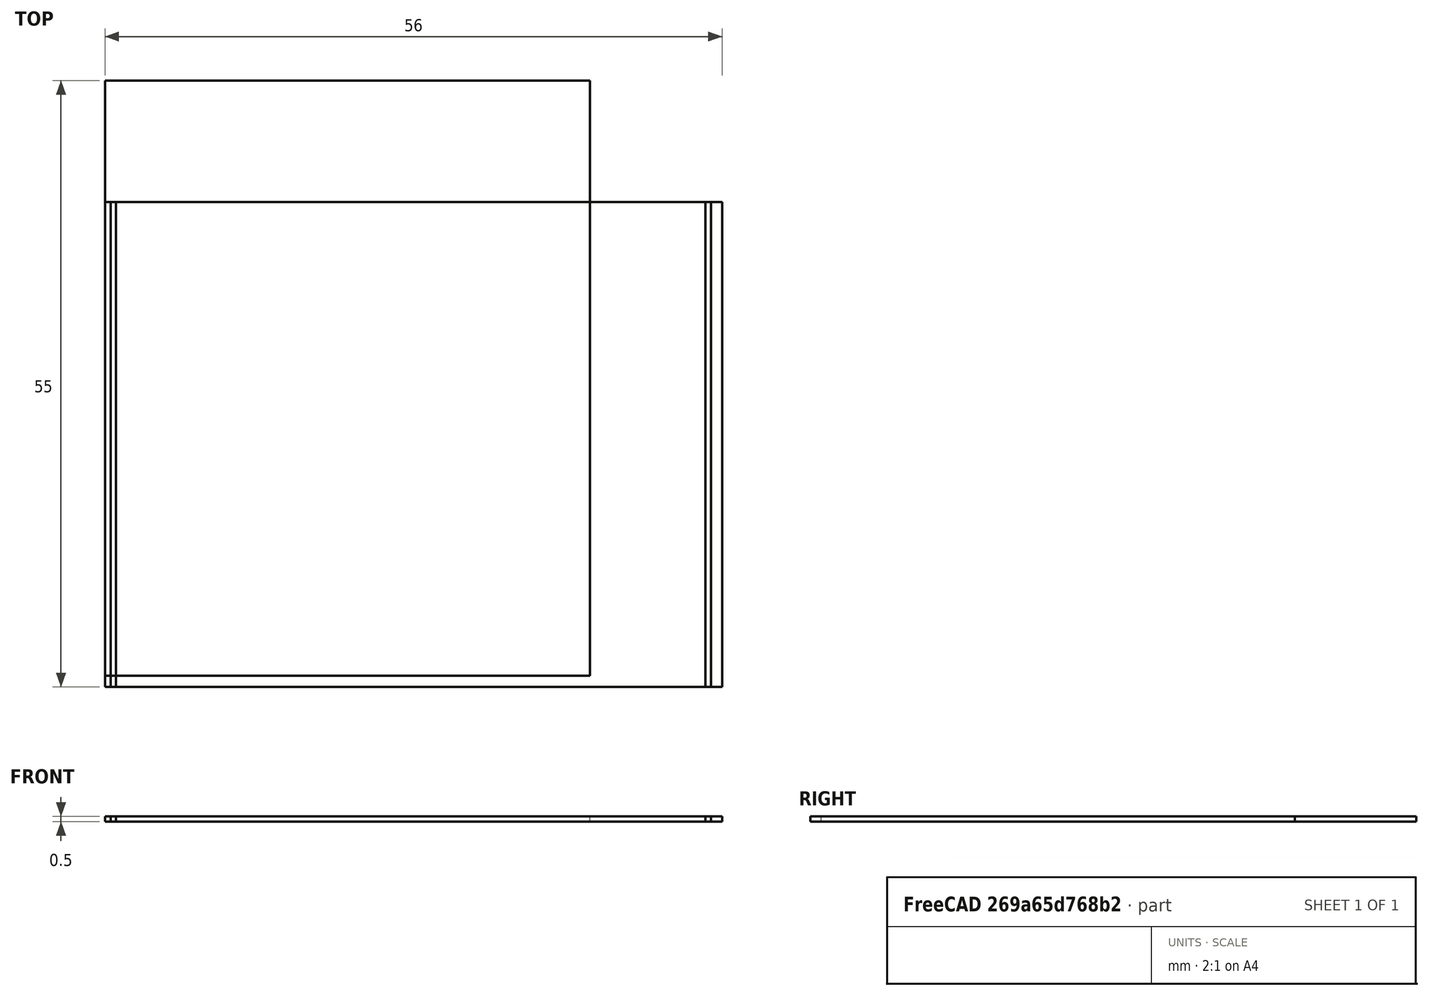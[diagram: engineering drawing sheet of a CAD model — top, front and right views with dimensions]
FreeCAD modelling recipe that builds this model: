
FCSTD DOCUMENT  (FreeCAD 1.0R39109 (Git))
Label: Tea_Light_Lithopane_MA_logo
License: All rights reserved
LicenseURL: http://www.ohwr.org/attachments/2388/cern_ohl_v_1_2.txt
objects: App::FeaturePython×8, Sketcher::SketchObject×4, PartDesign::Pad×4, PartDesign::Body×4, Mesh::Feature×4
note: 24 computed .brp shape members not serialized (recipe doc carries the construction recipe); baked Part::Feature solids carry a one-line shape summary decoded from their .brp

FEATURE [App::FeaturePython] ma_symbol_black  # WARN: FeaturePython — macro-defined, semantics opaque (R4)
  BaseHeight = 0.5
  LayerHeight = 0.1
  MaximumHeight = 3
  NozzleSize = 0.4
  Path = <userpath>/Documents/makersasylum/logos/ma-symbol-black.png
  UpdateNotifier = 2
  ppi = 747.889
FEATURE [Sketcher::SketchObject] Sketch
  ArcFitTolerance = 1e-06
  AttachmentSupport = -> [XY_Plane]
  FullyConstrained = true
  MakeInternals = false
  MapMode = 5
  sketch-geometry (4):
    g0: LineSegment StartX=-4 StartY=-11 StartZ=0 EndX=40 EndY=-11 EndZ=0
    g1: LineSegment StartX=40 StartY=-11 StartZ=0 EndX=40 EndY=43 EndZ=0
    g2: LineSegment StartX=40 StartY=43 StartZ=0 EndX=-4 EndY=43 EndZ=0
    g3: LineSegment StartX=-4 StartY=43 StartZ=0 EndX=-4 EndY=-11 EndZ=0
  constraints (12):
    c: Coincident(g0,g1)
    c: Coincident(g1,g2)
    c: Coincident(g2,g3)
    c: Horizontal(g0)
    c: Horizontal(g2)
    c: Vertical(g1)
    c: Vertical(g3)
    c: Distance(g1,g3) = 44
    c: Distance(g0,g2) = 54
    c: Coincident(g3,g0)
    c: DistanceX(g0,g-1) = 4
    c: DistanceY(g0,g-1) = 11
FEATURE [PartDesign::Pad] Pad
  Direction = (0,0,1)
  Length = 0.5
  Length2 = 10
  Profile = -> Sketch
  ReferenceAxis = -> Sketch [N_Axis]
  Refine = true
  Suppressed = false
  Type = 0
FEATURE [PartDesign::Body] Body
  AllowCompound = false
  Group = -> [Sketch,Pad]
  Origin = -> Origin
  Tip = -> Pad
FEATURE [Mesh::Feature] ma_symbol_black_Result
FEATURE [App::FeaturePython] ma_symbol_black_Mesh  # WARN: FeaturePython — macro-defined, semantics opaque (R4)
  LithophaneImage = -> ma_symbol_black
  Result = -> ma_symbol_black_Result
FEATURE [App::FeaturePython] make  # WARN: FeaturePython — macro-defined, semantics opaque (R4)
  BaseHeight = 0.5
  LayerHeight = 0.1
  MaximumHeight = 3
  NozzleSize = 0.4
  Path = <userpath>/Documents/3d_prints/2025_April/Lithopanes/make.png
  UpdateNotifier = 2
  ppi = 142.875
FEATURE [Sketcher::SketchObject] Sketch001
  ArcFitTolerance = 1e-06
  AttachmentSupport = -> [XY_Plane001]
  FullyConstrained = true
  MakeInternals = false
  MapMode = 5
  sketch-geometry (4):
    g0: LineSegment StartX=-3 StartY=32 StartZ=0 EndX=-3 EndY=-12 EndZ=0
    g1: LineSegment StartX=-3 StartY=-12 StartZ=0 EndX=51 EndY=-12 EndZ=0
    g2: LineSegment StartX=51 StartY=-12 StartZ=0 EndX=51 EndY=32 EndZ=0
    g3: LineSegment StartX=51 StartY=32 StartZ=0 EndX=-3 EndY=32 EndZ=0
  constraints (12):
    c: Coincident(g0,g1)
    c: Coincident(g1,g2)
    c: Coincident(g2,g3)
    c: Coincident(g3,g0)
    c: Vertical(g0)
    c: Vertical(g2)
    c: Horizontal(g1)
    c: Horizontal(g3)
    c: Distance(g0,g2) = 54
    c: Distance(g1,g3) = 44
    c: DistanceY(g0,g-1) = 12
    c: DistanceX(g0,g-1) = 3
FEATURE [PartDesign::Pad] Pad001
  Direction = (0,0,1)
  Length = 0.5
  Length2 = 10
  Profile = -> Sketch001
  ReferenceAxis = -> Sketch001 [N_Axis]
  Refine = true
  Suppressed = false
  Type = 0
FEATURE [PartDesign::Body] Body001
  AllowCompound = false
  Group = -> [Sketch001,Pad001]
  Origin = -> Origin001
  Tip = -> Pad001
FEATURE [Mesh::Feature] make_Result
FEATURE [App::FeaturePython] make_Mesh  # WARN: FeaturePython — macro-defined, semantics opaque (R4)
  LithophaneImage = -> make
  Result = -> make_Result
FEATURE [App::FeaturePython] break  # WARN: FeaturePython — macro-defined, semantics opaque (R4)
  BaseHeight = 0.5
  LayerHeight = 0.1
  MaximumHeight = 3
  NozzleSize = 0.4
  Path = <userpath>/Documents/3d_prints/2025_April/Lithopanes/break.png
  UpdateNotifier = 1
  ppi = 148.167
FEATURE [Sketcher::SketchObject] Sketch002
  ArcFitTolerance = 1e-06
  AttachmentSupport = -> [XY_Plane002]
  FullyConstrained = true
  MakeInternals = false
  MapMode = 5
  sketch-geometry (4):
    g0: LineSegment StartX=-4 StartY=-12 StartZ=0 EndX=52 EndY=-12 EndZ=0
    g1: LineSegment StartX=52 StartY=-12 StartZ=0 EndX=52 EndY=32 EndZ=0
    g2: LineSegment StartX=52 StartY=32 StartZ=0 EndX=-4 EndY=32 EndZ=0
    g3: LineSegment StartX=-4 StartY=32 StartZ=0 EndX=-4 EndY=-12 EndZ=0
  constraints (12):
    c: Coincident(g0,g1)
    c: Coincident(g1,g2)
    c: Coincident(g2,g3)
    c: Coincident(g3,g0)
    c: Horizontal(g0)
    c: Horizontal(g2)
    c: Vertical(g1)
    c: Vertical(g3)
    c: Distance(g1,g3) = 56
    c: Distance(g0,g2) = 44
    c: DistanceX(g0,g-1) = 4
    c: DistanceY(g0,g-1) = 12
FEATURE [PartDesign::Pad] Pad002
  Direction = (0,0,1)
  Length = 0.5
  Length2 = 10
  Profile = -> Sketch002
  ReferenceAxis = -> Sketch002 [N_Axis]
  Refine = true
  Suppressed = false
  Type = 0
FEATURE [PartDesign::Body] Body002
  AllowCompound = false
  Group = -> [Sketch002,Pad002]
  Origin = -> Origin002
  Tip = -> Pad002
FEATURE [Mesh::Feature] break_Result
FEATURE [App::FeaturePython] break_Mesh  # WARN: FeaturePython — macro-defined, semantics opaque (R4)
  LithophaneImage = -> break
  Result = -> break_Result
FEATURE [App::FeaturePython] create  # WARN: FeaturePython — macro-defined, semantics opaque (R4)
  BaseHeight = 0.5
  LayerHeight = 0.1
  MaximumHeight = 3
  NozzleSize = 0.4
  Path = <userpath>/Documents/3d_prints/2025_April/Lithopanes/create.png
  UpdateNotifier = 1
  ppi = 164.042
FEATURE [Sketcher::SketchObject] Sketch003
  ArcFitTolerance = 1e-06
  AttachmentSupport = -> [XY_Plane003]
  FullyConstrained = true
  MakeInternals = false
  MapMode = 5
  sketch-geometry (4):
    g0: LineSegment StartX=-3.5 StartY=-12 StartZ=0 EndX=50.5 EndY=-12 EndZ=0
    g1: LineSegment StartX=50.5 StartY=-12 StartZ=0 EndX=50.5 EndY=32 EndZ=0
    g2: LineSegment StartX=50.5 StartY=32 StartZ=0 EndX=-3.5 EndY=32 EndZ=0
    g3: LineSegment StartX=-3.5 StartY=32 StartZ=0 EndX=-3.5 EndY=-12 EndZ=0
  constraints (12):
    c: Coincident(g0,g1)
    c: Coincident(g1,g2)
    c: Coincident(g2,g3)
    c: Coincident(g3,g0)
    c: Horizontal(g0)
    c: Horizontal(g2)
    c: Vertical(g1)
    c: Vertical(g3)
    c: Distance(g1,g3) = 54
    c: Distance(g0,g2) = 44
    c: DistanceX(g0,g-1) = 3.5
    c: DistanceY(g0,g-1) = 12
FEATURE [PartDesign::Pad] Pad003
  Direction = (0,0,1)
  Length = 0.5
  Length2 = 10
  Profile = -> Sketch003
  ReferenceAxis = -> Sketch003 [N_Axis]
  Refine = true
  Suppressed = false
  Type = 0
FEATURE [PartDesign::Body] Body003
  AllowCompound = false
  Group = -> [Sketch003,Pad003]
  Origin = -> Origin003
  Tip = -> Pad003
FEATURE [Mesh::Feature] create_Result
FEATURE [App::FeaturePython] create_Mesh  # WARN: FeaturePython — macro-defined, semantics opaque (R4)
  LithophaneImage = -> create
  Result = -> create_Result
